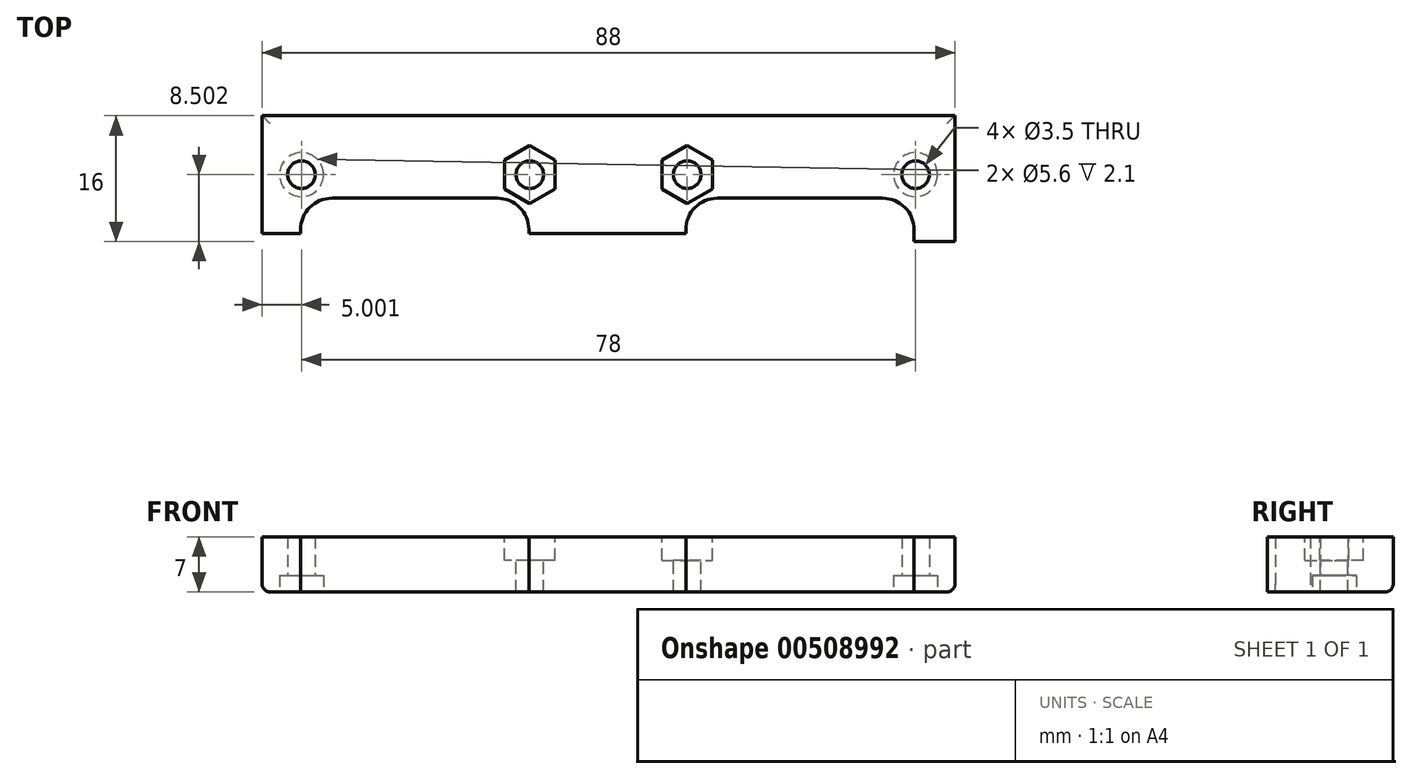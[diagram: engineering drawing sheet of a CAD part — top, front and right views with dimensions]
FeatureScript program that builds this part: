
annotation { "Feature Type Name" : "Feature", "Feature Type Description" : "" }
export const myFeature = defineFeature(function(context is Context, id is Id, definition is map)
    precondition{}
    {
        {
            var Q0;
            Q0=qCreatedBy(makeId("Top.planeOp"),FACE);
            var sketch = newSketch(context, id + "F0", { "sketchPlane" : qUnion([Q0])});
            skLineSegment(sketch, "E0.bottom", {"start": v(-39.43, 9.46) * mm, "end": v(48.57, 9.46) * mm});
            skLineSegment(sketch, "E0.left", {"start": v(-39.43, 9.46) * mm, "end": v(-39.43, -5.54) * mm});
            skLineSegment(sketch, "E0.right", {"start": v(48.57, 9.46) * mm, "end": v(48.57, -6.54) * mm});
            skPoint(sketch, "E1", {"position": v(-34.43, 1.96) * mm});
            skPoint(sketch, "E2", {"position": v(-5.43, 1.96) * mm});
            skPoint(sketch, "E3", {"position": v(14.57, 1.96) * mm});
            skPoint(sketch, "E4", {"position": v(43.57, 1.96) * mm});
            skLineSegment(sketch, "E5", {"start": v(-34.55, -5.54) * mm, "end": v(-34.55, -5.04) * mm});
            skLineSegment(sketch, "E6", {"start": v(-30.55, -1.04) * mm, "end": v(-9.55, -1.04) * mm});
            skLineSegment(sketch, "E7", {"start": v(-5.55, -5.04) * mm, "end": v(-5.55, -5.54) * mm});
            skLineSegment(sketch, "E8", {"start": v(14.39, -5.54) * mm, "end": v(14.39, -5.04) * mm});
            skPoint(sketch, "E8.endSnap0", {"position": v(-20.05, -1.04) * mm});
            skLineSegment(sketch, "E9", {"start": v(18.39, -1.04) * mm, "end": v(39.39, -1.04) * mm});
            skLineSegment(sketch, "E10", {"start": v(43.39, -5.04) * mm, "end": v(43.39, -6.54) * mm});
            skLineSegment(sketch, "E11", {"start": v(-39.43, -5.54) * mm, "end": v(-34.55, -5.54) * mm});
            skLineSegment(sketch, "E12", {"start": v(-5.55, -5.54) * mm, "end": v(14.39, -5.54) * mm});
            skLineSegment(sketch, "E13", {"start": v(43.39, -6.54) * mm, "end": v(48.57, -6.54) * mm});
            skPoint(sketch, "E14.visualSharp", {"position": v(-34.55, -1.04) * mm});
            skArc(sketch, "E14.filletArc", {"start": v(-30.55, -1.04) * mm, "mid": v(-33.38, -2.2) * mm, "end": v(-34.55, -5.04) * mm});
            skPoint(sketch, "E15.visualSharp", {"position": v(-5.55, -1.04) * mm});
            skArc(sketch, "E15.filletArc", {"start": v(-5.55, -5.04) * mm, "mid": v(-6.72, -2.2) * mm, "end": v(-9.55, -1.04) * mm});
            skPoint(sketch, "E16.visualSharp", {"position": v(14.39, -1.04) * mm});
            skArc(sketch, "E16.filletArc", {"start": v(18.39, -1.04) * mm, "mid": v(15.56, -2.2) * mm, "end": v(14.39, -5.04) * mm});
            skPoint(sketch, "E17.visualSharp", {"position": v(43.39, -1.04) * mm});
            skArc(sketch, "E17.filletArc", {"start": v(43.39, -5.04) * mm, "mid": v(42.22, -2.2) * mm, "end": v(39.39, -1.04) * mm});
            skSolve(sketch);
        }
        {
            var Q0;
            Q0 = qSketchRegion(id + "F0", true);
            extrude(context, id + "F1", {"entities" : qUnion([Q0]), "depth" : 7 * mm, "offsetDistance" : 25 * mm});
        }
        {
            var Q0;
            Q0=makeQuery(id+"F1.opExtrude","CAP_FACE",FACE,{"disambiguationData":[OSD([sQuery(id+"F0.wireOp",EDGE,"E0.bottom"),sQuery(id+"F0.wireOp",EDGE,"E0.top"),sQuery(id+"F0.wireOp",EDGE,"E0.left"),sQuery(id+"F0.wireOp",EDGE,"E0.right")])],"isStart":false});
            var sketch = newSketch(context, id + "F2", { "sketchPlane" : qUnion([Q0])});
            skPoint(sketch, "E18", {"position": v(-34.43, 1.96) * mm});
            skPoint(sketch, "E19", {"position": v(-5.43, 1.96) * mm});
            skPoint(sketch, "E20", {"position": v(14.57, 1.96) * mm});
            skPoint(sketch, "E21", {"position": v(43.57, 1.96) * mm});
            skCircle(sketch, "E22.cCircle", {"center": v(-5.43, 1.96) * mm, "radius": 3.2 * mm, "construction": true});
            skLineSegment(sketch, "E22.0", {"start": v(-8.63, 0.11) * mm, "end": v(-8.63, 3.8) * mm});
            skLineSegment(sketch, "E22.1", {"start": v(-8.63, 3.8) * mm, "end": v(-5.43, 5.66) * mm});
            skLineSegment(sketch, "E22.2", {"start": v(-5.43, 5.66) * mm, "end": v(-2.23, 3.8) * mm});
            skLineSegment(sketch, "E22.3", {"start": v(-2.23, 3.8) * mm, "end": v(-2.23, 0.11) * mm});
            skLineSegment(sketch, "E22.4", {"start": v(-2.23, 0.11) * mm, "end": v(-5.43, -1.73) * mm});
            skLineSegment(sketch, "E22.5", {"start": v(-5.43, -1.73) * mm, "end": v(-8.63, 0.11) * mm});
            skPoint(sketch, "E22.0.midPoint", {"position": v(-8.63, 1.96) * mm});
            skCircle(sketch, "E23.cCircle", {"center": v(14.57, 1.96) * mm, "radius": 3.2 * mm, "construction": true});
            skLineSegment(sketch, "E23.0", {"start": v(17.77, 3.8) * mm, "end": v(17.77, 0.11) * mm});
            skLineSegment(sketch, "E23.1", {"start": v(17.77, 0.11) * mm, "end": v(14.57, -1.73) * mm});
            skLineSegment(sketch, "E23.2", {"start": v(14.57, -1.73) * mm, "end": v(11.37, 0.11) * mm});
            skLineSegment(sketch, "E23.3", {"start": v(11.37, 0.11) * mm, "end": v(11.37, 3.8) * mm});
            skLineSegment(sketch, "E23.4", {"start": v(11.37, 3.8) * mm, "end": v(14.57, 5.66) * mm});
            skLineSegment(sketch, "E23.5", {"start": v(14.57, 5.66) * mm, "end": v(17.77, 3.8) * mm});
            skPoint(sketch, "E23.0.midPoint", {"position": v(17.77, 1.96) * mm});
            skSolve(sketch);
        }
        {
            var Q0;
            Q0=makeQuery(id+"F2.imprint","IMPRINT",FACE,{"disambiguationData":[TD([[makeQuery(id+"F2.imprint","IMPRINT",EDGE,{"derivedFrom":sQuery(id+"F2.wireOp",EDGE,"E23.0")}),-1.0]])]});
            var Q1;
            Q1=makeQuery(id+"F2.imprint","IMPRINT",FACE,{"disambiguationData":[TD([[makeQuery(id+"F2.imprint","IMPRINT",EDGE,{"derivedFrom":sQuery(id+"F2.wireOp",EDGE,"E22.0")}),-1.0]])]});
            extrude(context, id + "F3", {"entities" : qUnion([Q0, Q1]), "operationType" : NewBodyOperationType.REMOVE, "oppositeDirection" : true, "depth" : 3 * mm, "offsetDistance" : 25 * mm});
        }
        {
            var Q0;
            Q0=sQuery(id+"F2.wireOp",VERTEX,"E19");
            var Q1;
            Q1=sQuery(id+"F2.wireOp",VERTEX,"E20");
            var Q2;
            Q2=makeQuery(id+"F1.opExtrude","SWEPT_BODY",BODY,{"disambiguationData":[OSD([sQuery(id+"F0.wireOp",EDGE,"E0.bottom"),sQuery(id+"F0.wireOp",EDGE,"E0.top"),sQuery(id+"F0.wireOp",EDGE,"E0.left"),sQuery(id+"F0.wireOp",EDGE,"E0.right")])]});
            hole(context, id + "F4", {"style" : HoleStyle.SIMPLE, "endStyle" : HoleEndStyle.THROUGH, "holeDiameter" : 3.5 * mm, "isTappedThrough" : true, "tappedDepth" : 12 * mm, "tapClearance" : 3, "startFromSketch" : true, "locations" : qUnion([Q0, Q1]), "scope" : qUnion([Q2])});
        }
        {
            var Q0;
            Q0=makeQuery(id+"F1.opExtrude","CAP_EDGE",EDGE,{"disambiguationData":[OSD([sQuery(id+"F0.wireOp",EDGE,"E0.right")])],"isStart":true});
            var Q1;
            Q1=makeQuery(id+"F1.opExtrude","CAP_EDGE",EDGE,{"disambiguationData":[OSD([sQuery(id+"F0.wireOp",EDGE,"E0.bottom")])],"isStart":true});
            var Q2;
            Q2=makeQuery(id+"F1.opExtrude","CAP_EDGE",EDGE,{"disambiguationData":[OSD([sQuery(id+"F0.wireOp",EDGE,"E0.left")])],"isStart":true});
            var Q3;
            Q3=makeQuery(id+"F1.opExtrude","CAP_EDGE",EDGE,{"disambiguationData":[OSD([sQuery(id+"F0.wireOp",EDGE,"E0.top")])],"isStart":true});
            fillet(context, id + "F5", {"entities" : qUnion([Q0, Q1, Q2, Q3]), "radius" : 1 * mm, "tangentPropagation" : true, "allowEdgeOverflow" : false});
        }
        {
            var Q0;
            Q0=makeQuery(id+"F1.opExtrude","CAP_FACE",FACE,{"disambiguationData":[OSD([sQuery(id+"F0.wireOp",EDGE,"E0.bottom"),sQuery(id+"F0.wireOp",EDGE,"E0.left"),sQuery(id+"F0.wireOp",EDGE,"E0.right"),sQuery(id+"F0.wireOp",EDGE,"E5"),sQuery(id+"F0.wireOp",EDGE,"E6"),sQuery(id+"F0.wireOp",EDGE,"E7"),sQuery(id+"F0.wireOp",EDGE,"E8"),sQuery(id+"F0.wireOp",EDGE,"E9"),sQuery(id+"F0.wireOp",EDGE,"E10"),sQuery(id+"F0.wireOp",EDGE,"E11"),sQuery(id+"F0.wireOp",EDGE,"E12"),sQuery(id+"F0.wireOp",EDGE,"E13"),sQuery(id+"F0.wireOp",EDGE,"E14.filletArc"),sQuery(id+"F0.wireOp",EDGE,"E15.filletArc"),sQuery(id+"F0.wireOp",EDGE,"E16.filletArc"),sQuery(id+"F0.wireOp",EDGE,"E17.filletArc")])],"isStart":true});
            var sketch = newSketch(context, id + "F6", { "sketchPlane" : qUnion([Q0])});
            skLineSegment(sketch, "E24.0", {"start": v(-39.43, -9.46) * mm, "end": v(-39.43, 5.54) * mm});
            skLineSegment(sketch, "E25.0", {"start": v(48.57, -9.46) * mm, "end": v(-39.43, -9.46) * mm});
            skLineSegment(sketch, "E26.0", {"start": v(48.57, 6.54) * mm, "end": v(48.57, -9.46) * mm});
            skPoint(sketch, "E27", {"position": v(-34.43, -1.96) * mm});
            skPoint(sketch, "E28", {"position": v(43.57, -1.96) * mm});
            skSolve(sketch);
        }
        {
            var Q0;
            Q0=sQuery(id+"F6.wireOp",VERTEX,"E27");
            var Q1;
            Q1=sQuery(id+"F6.wireOp",VERTEX,"E28");
            var Q2;
            Q2=makeQuery(id+"F1.opExtrude","SWEPT_BODY",BODY,{"disambiguationData":[OSD([sQuery(id+"F0.wireOp",EDGE,"E0.bottom"),sQuery(id+"F0.wireOp",EDGE,"E0.left"),sQuery(id+"F0.wireOp",EDGE,"E0.right"),sQuery(id+"F0.wireOp",EDGE,"E5"),sQuery(id+"F0.wireOp",EDGE,"E6"),sQuery(id+"F0.wireOp",EDGE,"E7"),sQuery(id+"F0.wireOp",EDGE,"E8"),sQuery(id+"F0.wireOp",EDGE,"E9"),sQuery(id+"F0.wireOp",EDGE,"E10"),sQuery(id+"F0.wireOp",EDGE,"E11"),sQuery(id+"F0.wireOp",EDGE,"E12"),sQuery(id+"F0.wireOp",EDGE,"E13"),sQuery(id+"F0.wireOp",EDGE,"E14.filletArc"),sQuery(id+"F0.wireOp",EDGE,"E15.filletArc"),sQuery(id+"F0.wireOp",EDGE,"E16.filletArc"),sQuery(id+"F0.wireOp",EDGE,"E17.filletArc")])]});
            hole(context, id + "F7", {"style" : HoleStyle.C_BORE, "endStyle" : HoleEndStyle.THROUGH, "holeDiameter" : 3.5 * mm, "cBoreDiameter" : 5.6 * mm, "cBoreDepth" : 2.1 * mm, "isTappedThrough" : true, "tappedDepth" : 12 * mm, "tapClearance" : 3, "startFromSketch" : true, "locations" : qUnion([Q0, Q1]), "scope" : qUnion([Q2])});
        }
    });
